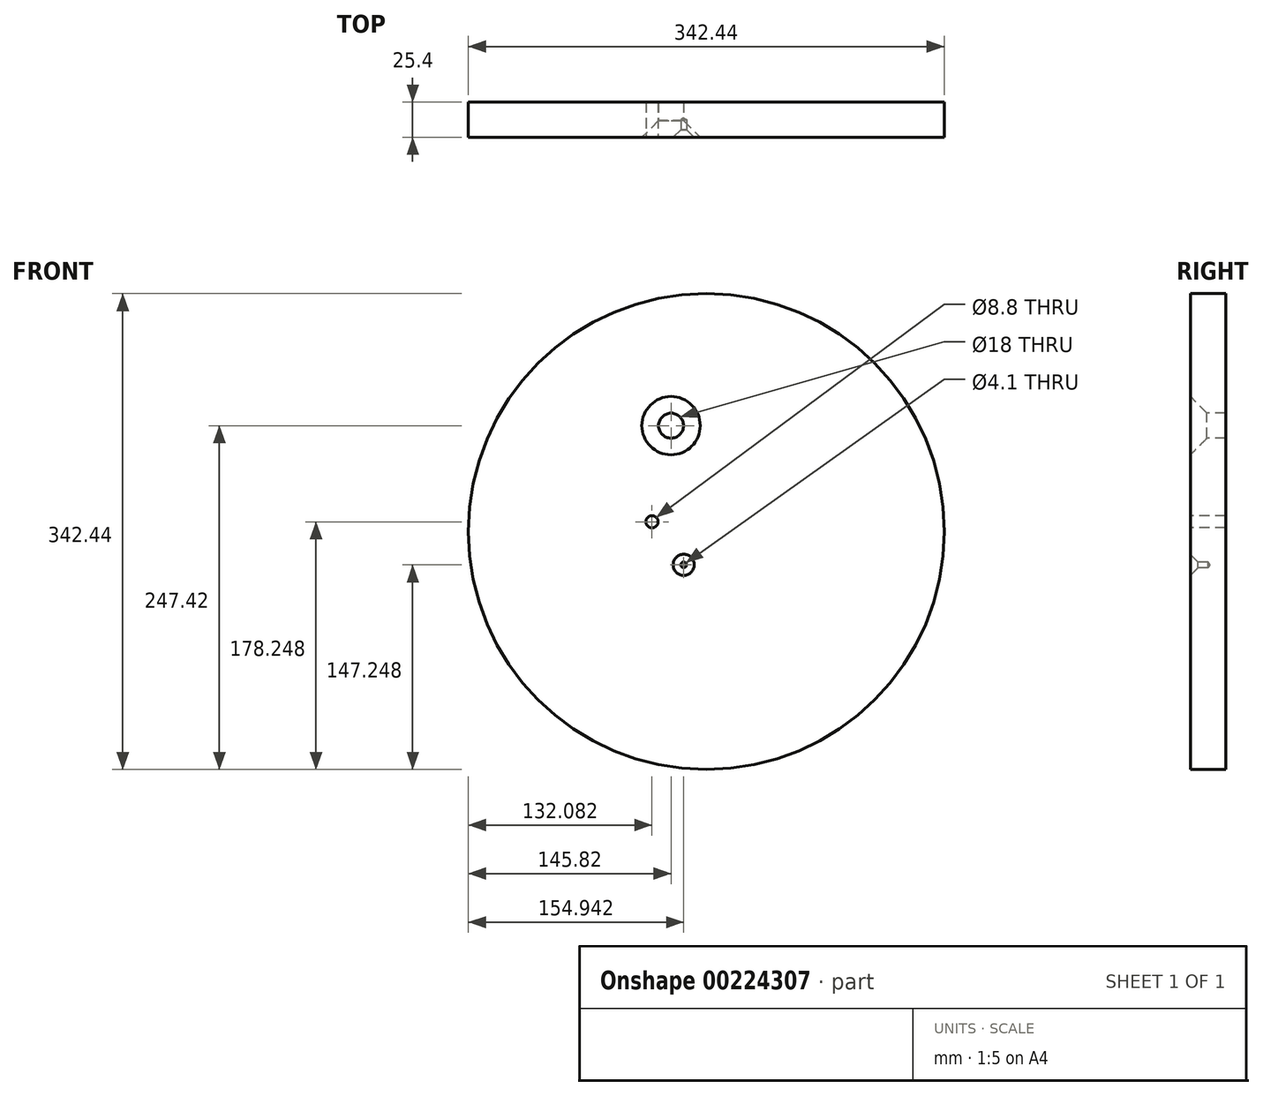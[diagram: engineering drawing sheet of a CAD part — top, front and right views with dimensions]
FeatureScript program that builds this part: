
annotation { "Feature Type Name" : "Feature", "Feature Type Description" : "" }
export const myFeature = defineFeature(function(context is Context, id is Id, definition is map)
    precondition{}
    {
        {
            var Q0;
            Q0=qCreatedBy(makeId("Front.planeOp"),FACE);
            var sketch = newSketch(context, id + "F0", { "sketchPlane" : qUnion([Q0])});
            skCircle(sketch, "E0", {"center": v(0, 0) * mm, "radius": 171.22 * mm});
            skSolve(sketch);
        }
        {
            var Q0;
            Q0=makeQuery(id+"F0.imprint","IMPRINT",FACE,{"disambiguationData":[TD([[makeQuery(id+"F0.imprint","IMPRINT",EDGE,{"derivedFrom":sQuery(id+"F0.wireOp",EDGE,"E0")}),1.0]])]});
            extrude(context, id + "F1", {"entities" : qUnion([Q0]), "depth" : 25.4 * mm});
        }
        {
            var Q0;
            Q0=makeQuery(id+"F1.opExtrude","CAP_FACE",FACE,{"disambiguationData":[OSD([sQuery(id+"F0.wireOp",EDGE,"E0")])],"isStart":false});
            var sketch = newSketch(context, id + "F2", { "sketchPlane" : qUnion([Q0])});
            skPoint(sketch, "E1", {"position": v(-39.14, 7.03) * mm});
            skPoint(sketch, "E2", {"position": v(45.64, 21.07) * mm});
            skPoint(sketch, "E3", {"position": v(33.76, -13.22) * mm});
            skPoint(sketch, "E4", {"position": v(-25.4, 76.2) * mm});
            skPoint(sketch, "E5", {"position": v(-16.28, -23.97) * mm});
            skPoint(sketch, "E6", {"position": v(7.74, -41.94) * mm});
            skSolve(sketch);
        }
        {
            var Q0;
            Q0=sQuery(id+"F2.wireOp",VERTEX,"E1");
            var Q1;
            Q1=makeQuery(id+"F1.opExtrude","SWEPT_BODY",BODY,{"disambiguationData":[OSD([sQuery(id+"F0.wireOp",EDGE,"E0")])]});
            hole(context, id + "F3", {"style" : HoleStyle.SIMPLE, "endStyle" : HoleEndStyle.THROUGH, "standardTappedOrClearance" : lookupTablePath({ "standard" : "ISO", "engagement" : "75%", "pitch" : "1.25 mm", "size" : "M10", "type" : "Tapped" }), "standardBlindInLast" : lookupTablePath({ "standard" : "ISO", "engagement" : "75%", "pitch" : "1.25 mm", "size" : "M10", "type" : "Tapped" }), "holeDiameter" : 8.8 * mm, "locations" : qUnion([Q0]), "scope" : qUnion([Q1]), "isTappedThrough" : true, "majorDiameter" : 10 * mm, "showTappedDepth" : true});
        }
        {
            var Q0;
            Q0=sQuery(id+"F2.wireOp",VERTEX,"E4");
            var Q1;
            Q1=makeQuery(id+"F1.opExtrude","SWEPT_BODY",BODY,{"disambiguationData":[OSD([sQuery(id+"F0.wireOp",EDGE,"E0")])]});
            hole(context, id + "F4", {"style" : HoleStyle.C_SINK, "endStyle" : HoleEndStyle.THROUGH, "standardTappedOrClearance" : lookupTablePath({ "standard" : "ISO", "engagement" : "75%", "pitch" : "2 mm", "size" : "M20", "type" : "Tapped" }), "standardBlindInLast" : lookupTablePath({ "standard" : "ISO", "engagement" : "75%", "pitch" : "2 mm", "size" : "M20", "type" : "Tapped" }), "holeDiameter" : 18 * mm, "cSinkDiameter" : 42 * mm, "cSinkAngle" : 90 * degree, "locations" : qUnion([Q0]), "scope" : qUnion([Q1]), "isTappedThrough" : true, "majorDiameter" : 20 * mm, "showTappedDepth" : true});
        }
        {
            var Q0;
            Q0=sQuery(id+"F2.wireOp",VERTEX,"E5");
            var Q1;
            Q1=makeQuery(id+"F1.opExtrude","SWEPT_BODY",BODY,{"disambiguationData":[OSD([sQuery(id+"F0.wireOp",EDGE,"E0")])]});
            hole(context, id + "F5", {"style" : HoleStyle.C_SINK, "endStyle" : HoleEndStyle.BLIND, "holeDiameter" : 4.1 * mm, "cSinkDiameter" : 15.2 * mm, "cSinkAngle" : 90 * degree, "holeDepth" : 12.7 * mm, "locations" : qUnion([Q0]), "scope" : qUnion([Q1])});
        }
    });
